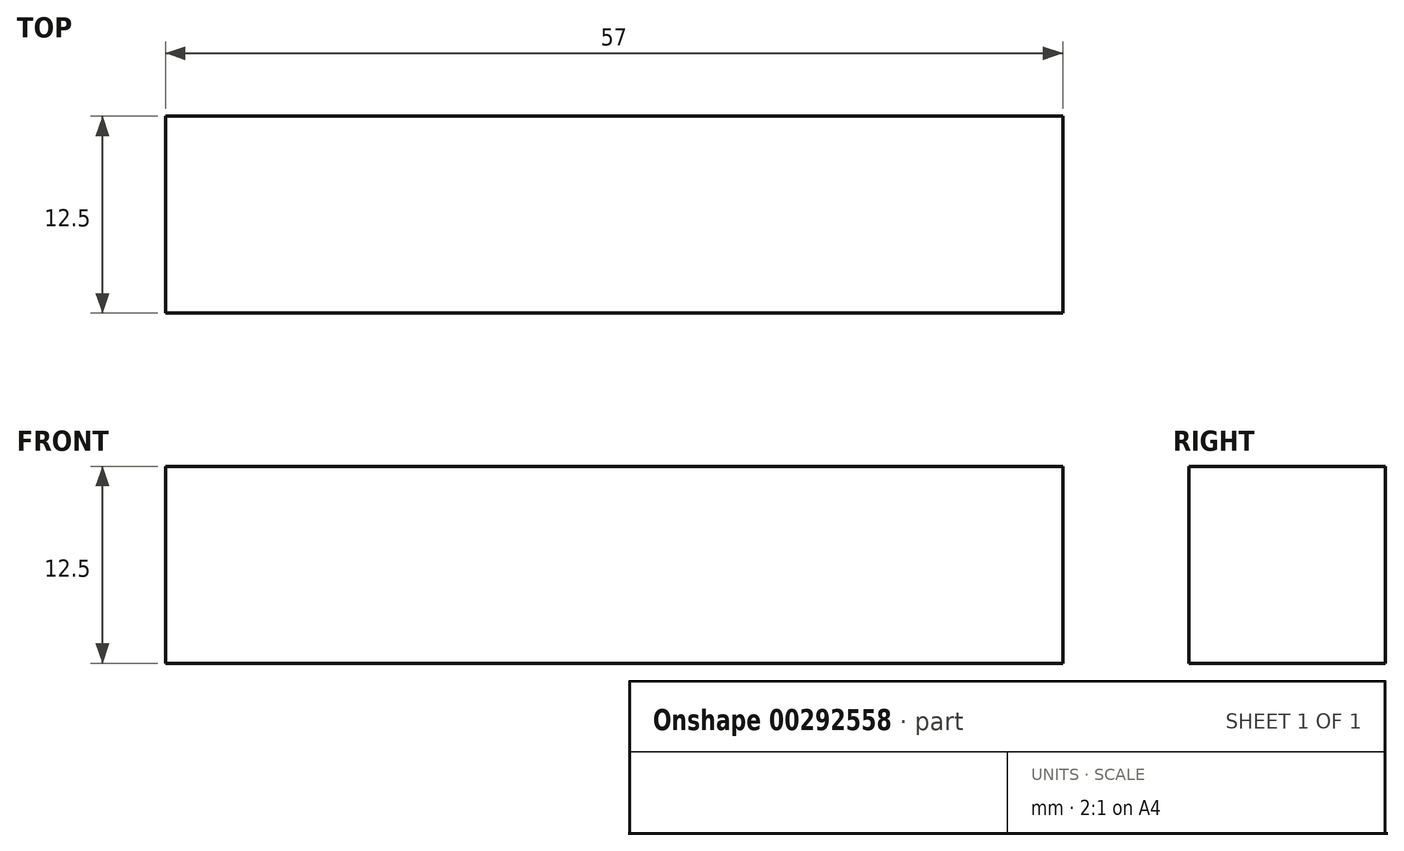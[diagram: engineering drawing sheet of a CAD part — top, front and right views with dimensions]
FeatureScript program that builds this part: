
annotation { "Feature Type Name" : "Feature", "Feature Type Description" : "" }
export const myFeature = defineFeature(function(context is Context, id is Id, definition is map)
    precondition{}
    {
        {
            var Q0;
            Q0=qCreatedBy(makeId("Front.planeOp"),FACE);
            var sketch = newSketch(context, id + "F0", { "sketchPlane" : qUnion([Q0])});
            skLineSegment(sketch, "E0.bottom", {"start": v(-26.04, 6.61) * mm, "end": v(30.96, 6.61) * mm});
            skLineSegment(sketch, "E0.top", {"start": v(-26.04, -5.89) * mm, "end": v(30.96, -5.89) * mm});
            skLineSegment(sketch, "E0.left", {"start": v(-26.04, 6.61) * mm, "end": v(-26.04, -5.89) * mm});
            skLineSegment(sketch, "E0.right", {"start": v(30.96, 6.61) * mm, "end": v(30.96, -5.89) * mm});
            skSolve(sketch);
        }
        {
            var Q0;
            Q0 = qSketchRegion(id + "F0", true);
            extrude(context, id + "F1", {"entities" : qUnion([Q0]), "depth" : 12.5 * mm});
        }
    });
